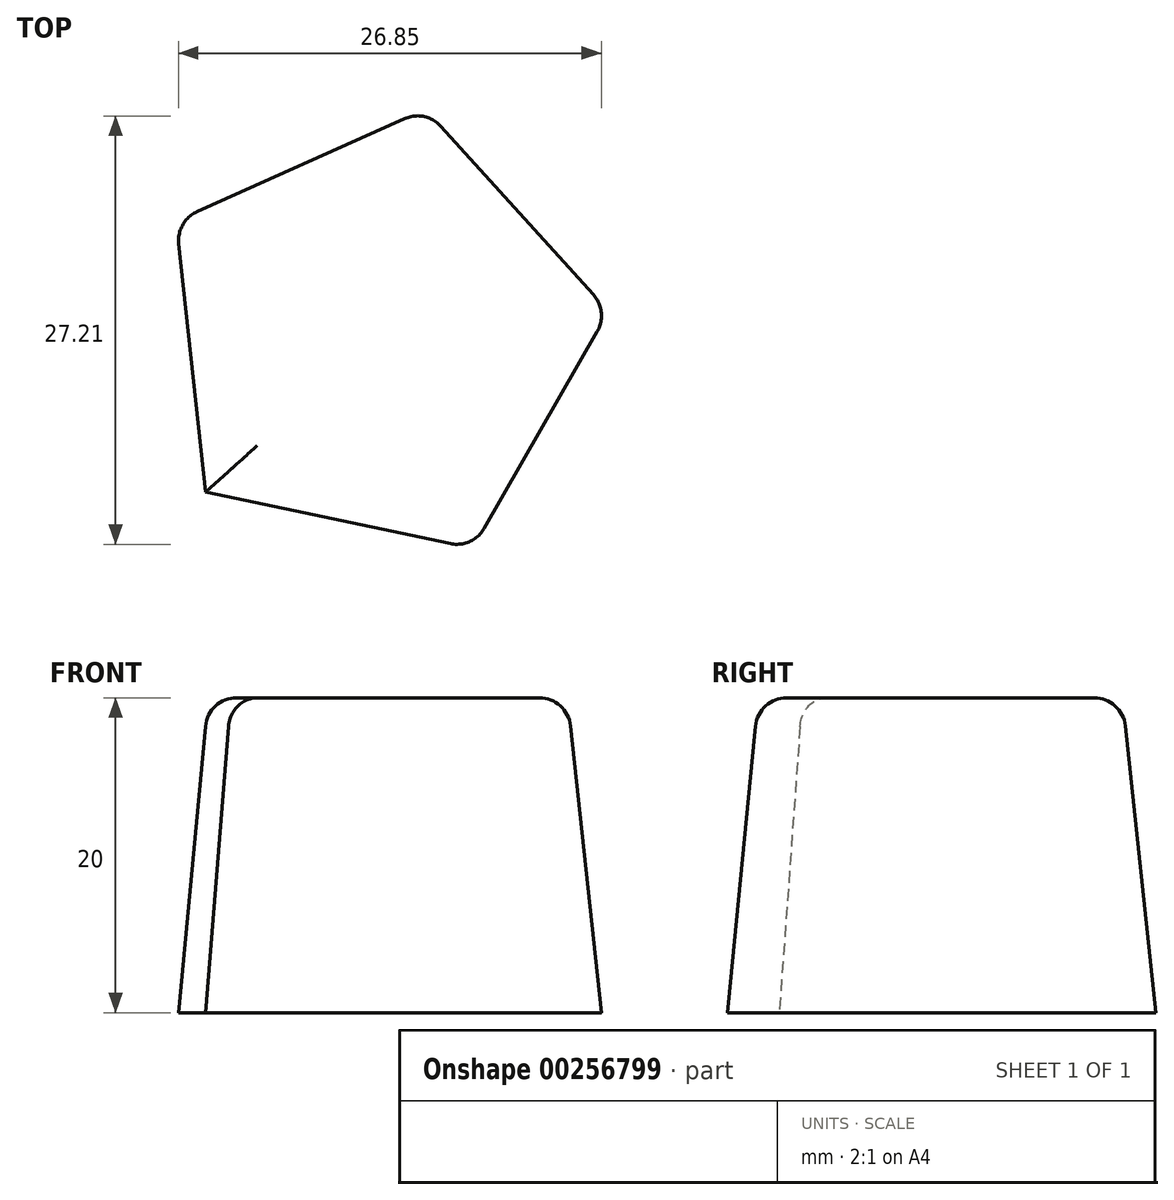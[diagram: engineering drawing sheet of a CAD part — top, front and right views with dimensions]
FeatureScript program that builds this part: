
annotation { "Feature Type Name" : "Feature", "Feature Type Description" : "" }
export const myFeature = defineFeature(function(context is Context, id is Id, definition is map)
    precondition{}
    {
        {
            var Q0;
            Q0=qCreatedBy(makeId("Top.planeOp"),FACE);
            var sketch = newSketch(context, id + "F0", { "sketchPlane" : qUnion([Q0])});
            skCircle(sketch, "E0.cCircle", {"center": v(0, 0) * mm, "radius": 11.93 * mm, "construction": true});
            skLineSegment(sketch, "E0.0", {"start": v(14.66, 1.58) * mm, "end": v(6.03, -13.46) * mm});
            skLineSegment(sketch, "E0.1", {"start": v(6.03, -13.46) * mm, "end": v(-10.93, -9.9) * mm});
            skLineSegment(sketch, "E0.2", {"start": v(-10.93, -9.9) * mm, "end": v(-12.79, 7.34) * mm});
            skLineSegment(sketch, "E0.3", {"start": v(-12.79, 7.34) * mm, "end": v(3.03, 14.43) * mm});
            skLineSegment(sketch, "E0.4", {"start": v(3.03, 14.43) * mm, "end": v(14.66, 1.58) * mm});
            skPoint(sketch, "E0.0.midPoint", {"position": v(10.35, -5.94) * mm});
            skSolve(sketch);
        }
        {
            var Q0;
            Q0=qSketchRegion(id+"F0",true);
            extrude(context, id + "F1", {"entities" : qUnion([Q0]), "depth" : 20 * mm, "hasDraft" : true, "draftAngle" : 5 * degree, "draftPullDirection" : true});
        }
        {
            var Q0;
            Q0=makeQuery(id+"F1.opExtrude","CAP_EDGE",EDGE,{"disambiguationData":[OSD([sQuery(id+"F0.wireOp",EDGE,"E0.3")])],"isStart":false});
            var Q1;
            Q1=makeQuery(id+"F1.opExtrude","CAP_EDGE",EDGE,{"disambiguationData":[OSD([sQuery(id+"F0.wireOp",EDGE,"E0.4")])],"isStart":false});
            var Q2;
            Q2=makeQuery(id+"F1.opExtrude","CAP_EDGE",EDGE,{"disambiguationData":[OSD([sQuery(id+"F0.wireOp",EDGE,"E0.2")])],"isStart":false});
            var Q3;
            Q3=makeQuery(id+"F1.opExtrude","CAP_EDGE",EDGE,{"disambiguationData":[OSD([sQuery(id+"F0.wireOp",EDGE,"E0.0")])],"isStart":false});
            var Q4;
            Q4=makeQuery(id+"F1.opExtrude","CAP_EDGE",EDGE,{"disambiguationData":[OSD([sQuery(id+"F0.wireOp",EDGE,"E0.1")])],"isStart":false});
            var Q5;
            Q5=makeQuery(id+"F1.opExtrude","SWEPT_EDGE",EDGE,{"disambiguationData":[OSD([sQuery(id+"F0.wireOp",EDGE,"E0.3"),sQuery(id+"F0.wireOp",EDGE,"E0.4")])]});
            var Q6;
            Q6=makeQuery(id+"F1.opExtrude","SWEPT_EDGE",EDGE,{"disambiguationData":[OSD([sQuery(id+"F0.wireOp",EDGE,"E0.0"),sQuery(id+"F0.wireOp",EDGE,"E0.4")])]});
            var Q7;
            Q7=makeQuery(id+"F1.opExtrude","SWEPT_EDGE",EDGE,{"disambiguationData":[OSD([sQuery(id+"F0.wireOp",EDGE,"E0.2"),sQuery(id+"F0.wireOp",EDGE,"E0.3")])]});
            var Q8;
            Q8=makeQuery(id+"F1.opExtrude","SWEPT_EDGE",EDGE,{"disambiguationData":[OSD([sQuery(id+"F0.wireOp",EDGE,"E0.0"),sQuery(id+"F0.wireOp",EDGE,"E0.1")])]});
            fillet(context, id + "F2", {"entities" : qUnion([Q0, Q1, Q2, Q3, Q4, Q5, Q6, Q7, Q8]), "radius" : 2 * mm, "tangentPropagation" : true, "allowEdgeOverflow" : false});
        }
    });
